# Revit family: Deca_Caixa acoplada com acionamento Duo_Lk_CD.23F
name_source: partatom
category: Plumbing Fixtures
units: mm (PartAtom-declared; Revit-internal decimal feet)

## family parameters
Cut with Voids When Loaded = No
Host = Face
Part Type = Normal
Room Calculation Point = No
Round Connector Dimension = Use Radius
Shared = Yes

## types (5) — shared parameters
Acompanha o Produto = Conjunto de Mecanismos (torre de entrada + Torre de saída) + Conjunto de Fixação da Caixa Acoplada + Botão Acionamento
Aprovado por = quattroD
Atendimento ao Cliente = 0800-0117073
Categoria = BACIAS E BIDES
Composição Anel Vedação = -
Composição Assento = -
Composição Básica = Argila, feldspato, caulim, vidrados e corantes inorgânicos.
Composição Componente = Liga de elastômeros e plásticos de engenharia.
Consumo = 6 / 3 (lpf) - 1,6 / 0,8 (gpf)
Cor Interna = -
Cor Secundária = -
Cores Componente = Cromado
Criado por = quattroD
Código Pai = CD.23F
Description = Caixa acoplada com acionamento Duo
Informações Complementares = -
Itens de Instalação = -
Linha = LK
Manufacturer = Deca
Norma = NBR15491
Peso Líquido (Kg) = 14.438
Pressão máx. funcionamento = 40 MCA
Pressão mín. Aquec. Acúmulo = -
Pressão mín. Aquec. Passagem = -
Pressão mín. funcionamento = 2 MCA
Saída de Esgoto = -
Segmento = Banheiro Luxo
Tipo de dispositivo economizador = -
Tipo de mecanismo utilizado = -
Tipo de rosca de entrada = -
Tipo de rosca de saída = -
URL = www.deca.com.br
Vazão na Pressão máx. (L/min) = -
Vazão na Pressão mín. (L/min) = -
zero-valued in all types: Default Elevation

## per-type parameters (varying)
| type | Cor Principal | Material | Model |
| CD.23F.17_Branco | Branco | Deca_Branco | CD.23F.17 |
| CD.23F.22_Marrom Fosco | Marrom fosco | Deca_Marrom Fosco | CD.23F.22 |
| CD.23F.86_Cinza Fosco | Cinza fosco | Deca_Cinza Fosco | CD.23F.86 |
| CD.23F.94_Ébano Fosco | Ébano fosco | Deca_Ébano Fosco | CD.23F.94 |
| CD.23F.95_Ébano | Ébano | Deca_Ébano | CD.23F.95 |

## geometry (parser evidence)
native form markers: Sweep x2
no freeform markers — native parametric forms only
